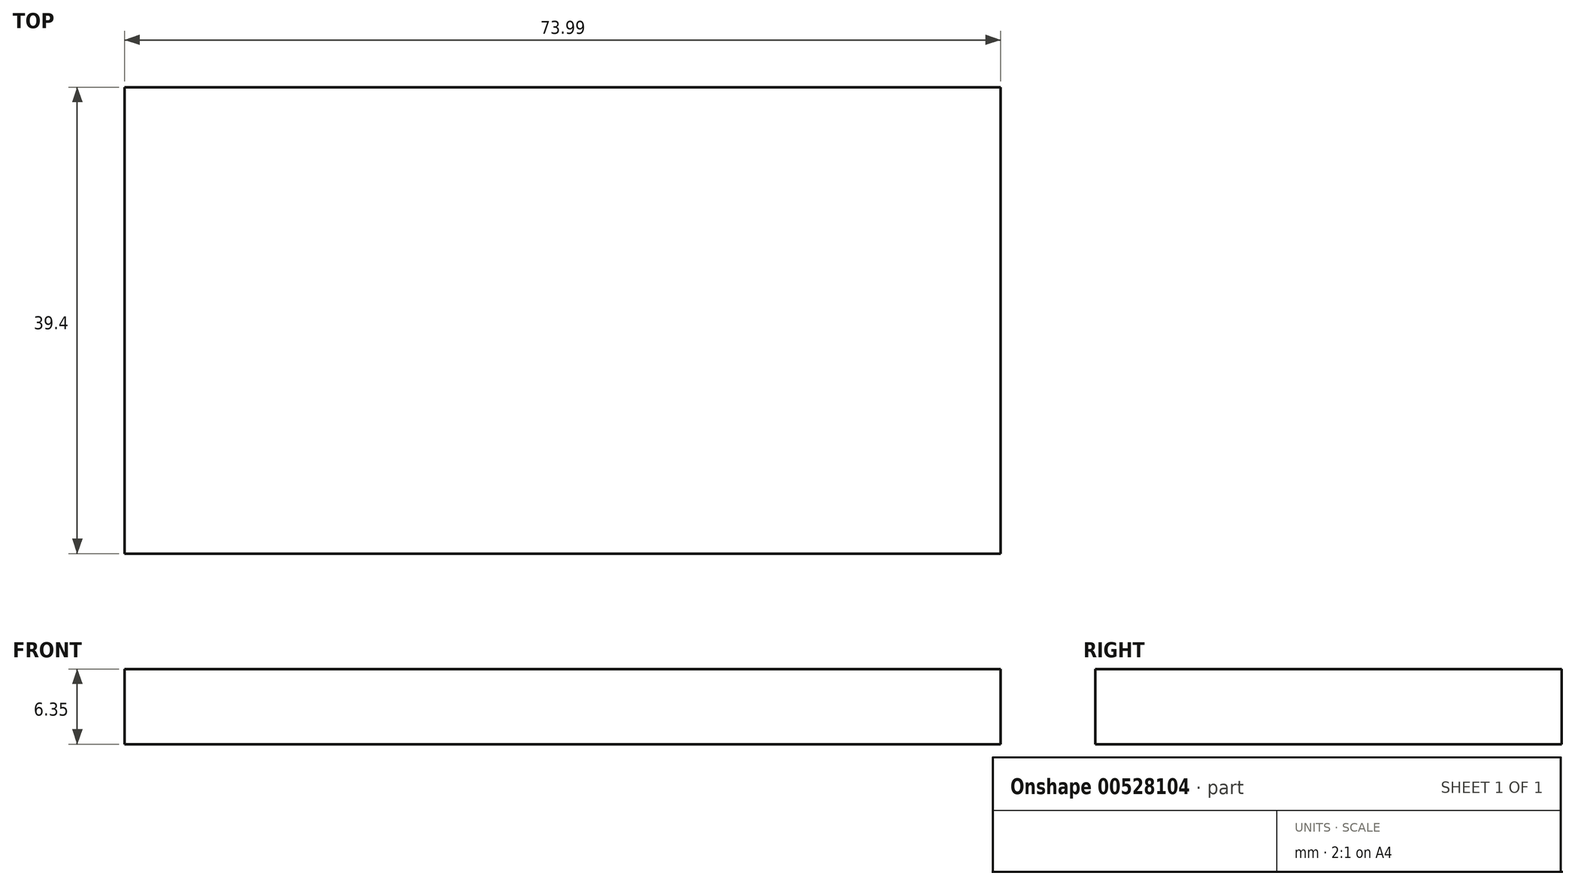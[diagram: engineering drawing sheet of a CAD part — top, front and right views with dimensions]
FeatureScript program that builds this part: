
annotation { "Feature Type Name" : "Feature", "Feature Type Description" : "" }
export const myFeature = defineFeature(function(context is Context, id is Id, definition is map)
    precondition{}
    {
        {
            var Q0;
            Q0=qCreatedBy(makeId("Top.planeOp"),FACE);
            var sketch = newSketch(context, id + "F0", { "sketchPlane" : qUnion([Q0])});
            skLineSegment(sketch, "E0.bottom", {"start": v(-28.57, 19.85) * mm, "end": v(45.42, 19.85) * mm});
            skLineSegment(sketch, "E0.top", {"start": v(-28.57, -19.55) * mm, "end": v(45.42, -19.55) * mm});
            skLineSegment(sketch, "E0.left", {"start": v(-28.57, 19.85) * mm, "end": v(-28.57, -19.55) * mm});
            skLineSegment(sketch, "E0.right", {"start": v(45.42, 19.85) * mm, "end": v(45.42, -19.55) * mm});
            skSolve(sketch);
        }
        {
            var Q0;
            Q0=makeQuery(id+"F0.imprint","IMPRINT",FACE,{"disambiguationData":[TD([[makeQuery(id+"F0.imprint","IMPRINT",EDGE,{"derivedFrom":sQuery(id+"F0.wireOp",EDGE,"E0.bottom")}),-1.0]])]});
            var Q1;
            Q1=makeQuery(id+"F0.imprint","IMPRINT",FACE,{"disambiguationData":[TD([[makeQuery(id+"F0.imprint","IMPRINT",EDGE,{"derivedFrom":sQuery(id+"F0.wireOp",EDGE,"E0.bottom")}),-1.0]])]});
            extrude(context, id + "F1", {"entities" : qUnion([Q0, Q1]), "depth" : 6.35 * mm, "offsetDistance" : 25.4 * mm});
        }
    });
